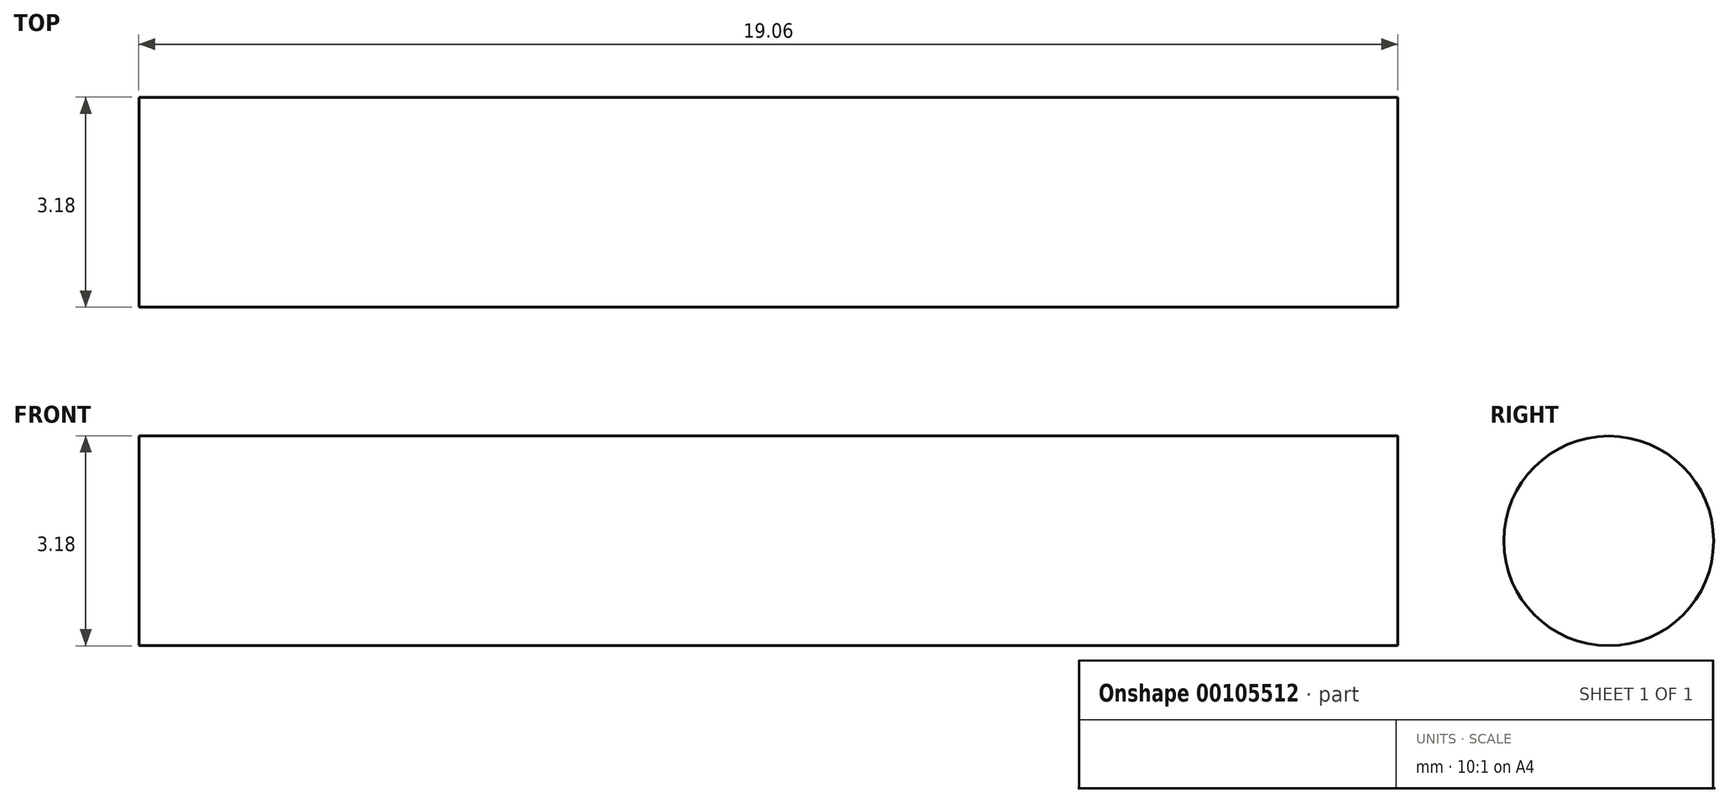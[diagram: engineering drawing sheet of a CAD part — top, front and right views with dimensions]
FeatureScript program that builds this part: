
annotation { "Feature Type Name" : "Feature", "Feature Type Description" : "" }
export const myFeature = defineFeature(function(context is Context, id is Id, definition is map)
    precondition{}
    {
        {
            var Q0;
            Q0=qCreatedBy(makeId("Right.planeOp"),FACE);
            var sketch = newSketch(context, id + "F0", { "sketchPlane" : qUnion([Q0])});
            skCircle(sketch, "E0", {"center": v(0, 0) * mm, "radius": 1.59 * mm});
            skSolve(sketch);
        }
        {
            var Q0;
            Q0=makeQuery(id+"F0.imprint","IMPRINT",FACE,{"disambiguationData":[TD([[makeQuery(id+"F0.imprint","IMPRINT",EDGE,{"derivedFrom":sQuery(id+"F0.wireOp",EDGE,"E0")}),1.0]])]});
            extrude(context, id + "F1", {"entities" : qUnion([Q0]), "endBound" : BoundingType.SYMMETRIC, "depth" : 19.05 * mm});
        }
    });
